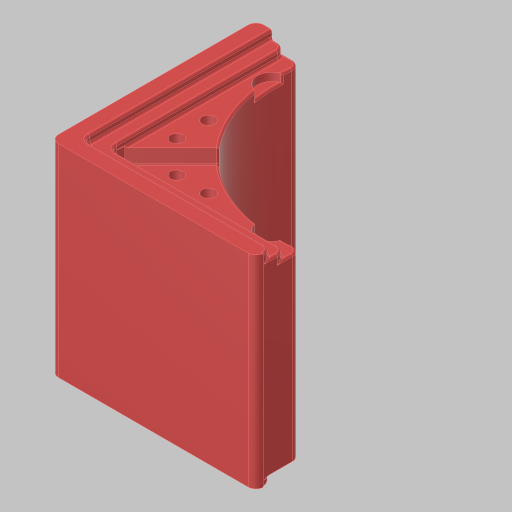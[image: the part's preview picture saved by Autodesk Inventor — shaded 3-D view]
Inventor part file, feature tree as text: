
AUTODESK INVENTOR PART (.ipt)
format: ipt  version: 2023.5 (Build 275446000, 446)  size: 438,784 bytes
history: native  units: in
note: dims shown in document units (in); Inventor stores cm internally (conversion verified against a paired STEP export)
features: extrude x8, sketch x7, projected_geometry x6, fillet x2, hole x1
ambient origin geometry x8: Origin, YZ Plane, XZ Plane, XY Plane, X Axis, Y Axis, Z Axis, Center Point
bodies: Solid1 (feature_tree)
feature tree (24):
  sketch  "Sketch1"  dims[d0=1.0in d1=1.0in]
  extrude  "Extrusion1"  Depth=1.0in
  hole  "Hole1"  [1 undecoded]
  extrude  "Extrusion2"  Depth=0.5in
  extrude  "Extrusion3"  Depth=2.125in
  extrude  "Extrusion4"  Depth=0.25in
  fillet  "Fillet1"  Radius=0.25in
  extrude  "Extrusion5"  Depth=0.3937in
  sketch  "Sketch6"  dims[d12=1.9685in d14=0.5in d15=0.3937in d17=1.0in d19=1.9685in d21=0.5in d22=0.3937in d24=1.0in]
  extrude  "Extrusion6"  Depth=0.0312in
  extrude  "Extrusion7"  Depth=0.0312in
  extrude  "Extrusion8"  Depth=0.0312in TaperAngle=0.0deg
  fillet  "Fillet2"  Radius=0.249in
  sketch  "Sketch2"  dims[d2=3.0in d3=3.0in]
  sketch  "Sketch3"  dims[d4=4.375in d5=0.5in]
  sketch  "Sketch4"  dims[d6=0.5in d7=2.125in]
  sketch  "Sketch5"  dims[d9=2.125in d10=0.25in d11=0.25in]
  projected_geometry  "Projected Loop1"
  projected_geometry  "Projected Loop2"
  projected_geometry  "Projected Loop3"
  sketch  "Sketch7"  dims[d26=2.837in d27=0.0in d28=0.201in d29=0.75in d30=0.563in d31=0.12in d32=0.5635in d33=0.2362in d34=0.0in d35=0.375in d36=0.1in d37=0.12in d38=0.0in d39=0.249in d40=0.249in d41=0.124in d42=0.0in d43=0.249in d44=0.249in d45=0.124in d46=0.0in d47=0.125in d48=0.35in d49=0.25in d50=0.0in d51=0.0312in d52=0.25in d53=0.0in d54=1.0in d55=0.0in d56=0.45in d57=0.45in d58=0.125in d59=0.0in]
  projected_geometry  "Project Cut Edges1"
  projected_geometry  "Project Cut Edges2"
  projected_geometry  "Project Cut Edges3"
note: 1 required parameter value undecoded (feature->parameter linkage not recoverable at this tier; creation-order binding heuristic only, values carry confidence <= 0.55)
